# Revit family: hb_710_501050_002_1d2a
name_source: partatom
category: Lighting Fixtures
units: mm (PartAtom-declared; Revit-internal decimal feet)

## family parameters
Cut with Voids When Loaded = No
Host = Face
Light Source = No
Part Type = Normal
Room Calculation Point = No
Round Connector Dimension = Use Diameter
Shared = No

## types (1)
- MultiLumen 2 (1 x LED Modul 840, 1100 lm, 4000)
    Apparent Load = 10 VA
    CIE Flux Codes = 41 70 90 91 100
    Color Rendering = 80
    Color Temperature = 4000
    Default Elevation = 1800 mm
    Description = Series: HB 710
Oval luminaire in classic design. Housing and diffusor: opal, made of shockproof plastic (polycarbonate). Internal fixing points mean no screws are visible. MultiLumen: 2 steps adjustable luminous flux. Factory setting is the highest luminous flux. Simple, tool-free installation using the Plug+Play plug-in system. LED module can be connected without use of tools. Convenient, flexible connection option using 2 rear and 4 lateral cable inlets. Suitable for through-wiring. Luminaire with limited surface temperature in accordance with EN  60598-2-24 for use in environments in which a deposit of non-conductive dust on the luminaire can be expected. 
Colour: white
Length: 207 mm
Width: 97 mm
Height: 56 mm
Lamp: LED
Colour temperature: 4000K
Colour rendering index (CRI): 80
System power: 9.5 W
Rated luminous flux: 1100 lm
Luminous efficiency: 116 lm/W
System power 2: 6 W
Rated luminous flux 2: 700 lm
Luminous efficiency 2: 117 lm/W
Control gear: EB
Protection class: II
Type of protection: IP 54
    Height = 56 mm
    Lamp = 1 x LED Modul 840
    Lamp Light Flux = 1100 lm
    Lamp count = 1
    Length = 207 mm
    Lifetime = 50000 h
    Luminous efficacy = 116 lm/W
    Manufacturer = RZB
    ModVariant = No
    Model = 501050.002
    Mounting Place = Ceiling, Wall
    Mounting Type = Surface mounted
    Number of Poles = 1
    OnlyDefault = Yes
    Power Factor = 1
    Product Name = HB 710
    Product group = Surface mounted ceiling and wall luminaires
    ProductGroupID = 305
    Protection Class = Protection class II
    Protection Degree = IP 54
    RLX_Detail_Level = 1
    RLX_Emergency_Light_Flux = 0 lm
    RLX_Emergency_Type = 0
    RLX_Emergency_Type_DB = No
    RlxData = <blob elided: 79933 chars, md5=3ebef4da>
    Socket = socket
    Standby Power = 0 W
    System Light Flux = 1100 lm
    System Power = 10 W
    Type Comments = MultiLumen 2
    Type Image = 501050.002.jpg
    URL = http://relux.com
    VarID = multilumen_2
    Voltage = 230 V
    Voltage Range = 220-240 V
    Weight = 0.00 kg
    Width = 97 mm

## geometry (parser evidence)
native form markers: Sweep x12
no freeform markers — native parametric forms only
